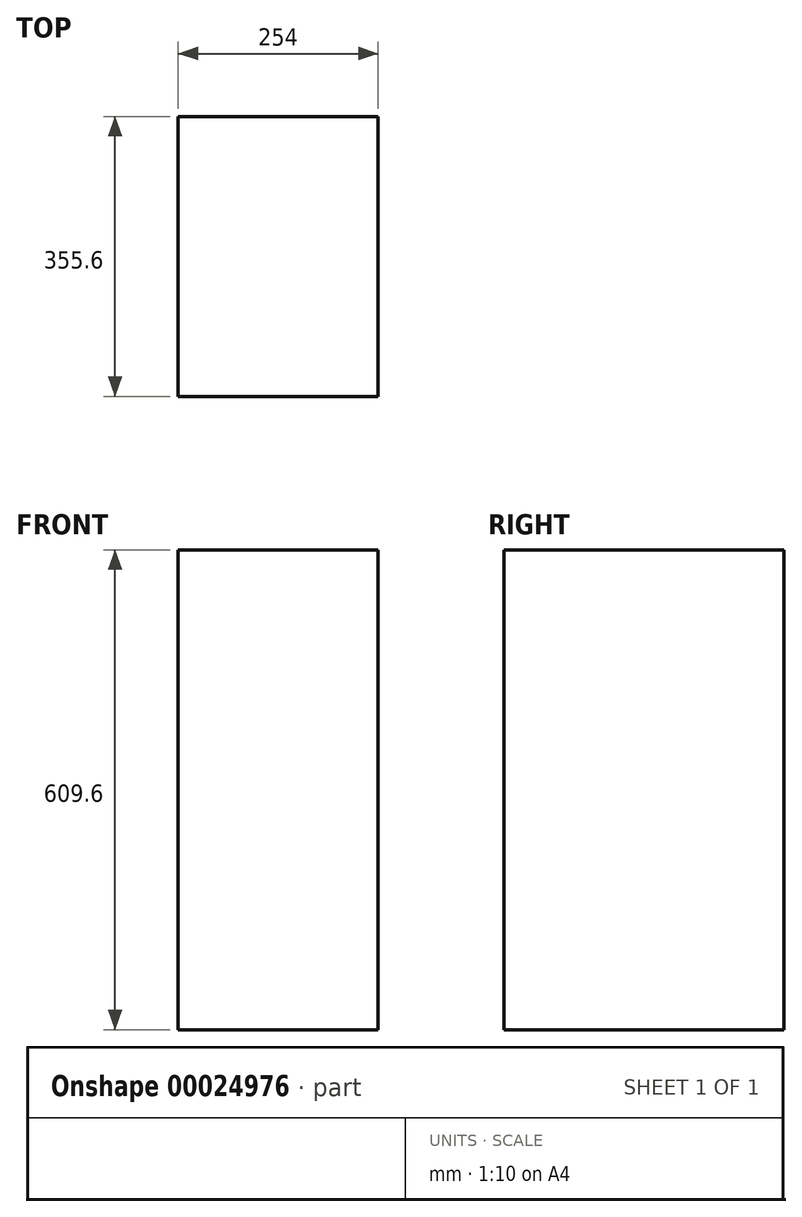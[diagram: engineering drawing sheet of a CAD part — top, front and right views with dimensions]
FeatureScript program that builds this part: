
annotation { "Feature Type Name" : "Feature", "Feature Type Description" : "" }
export const myFeature = defineFeature(function(context is Context, id is Id, definition is map)
    precondition{}
    {
        {
            var Q0;
            Q0=qCreatedBy(makeId("Front.planeOp"),FACE);
            var sketch = newSketch(context, id + "F0", { "sketchPlane" : qUnion([Q0])});
            skLineSegment(sketch, "E0.bottom", {"start": v(-116.58, 557.77) * mm, "end": v(137.42, 557.77) * mm});
            skLineSegment(sketch, "E0.top", {"start": v(-116.58, -51.83) * mm, "end": v(137.42, -51.83) * mm});
            skLineSegment(sketch, "E0.left", {"start": v(-116.58, 557.77) * mm, "end": v(-116.58, -51.83) * mm});
            skLineSegment(sketch, "E0.right", {"start": v(137.42, 557.77) * mm, "end": v(137.42, -51.83) * mm});
            skSolve(sketch);
        }
        {
            var Q0;
            Q0=makeQuery(id+"F0.imprint","IMPRINT",FACE,{"disambiguationData":[TD([[makeQuery(id+"F0.imprint","IMPRINT",EDGE,{"derivedFrom":sQuery(id+"F0.wireOp",EDGE,"E0.bottom")}),-1.0]])]});
            extrude(context, id + "F1", {"entities" : qUnion([Q0]), "depth" : 355.6 * mm});
        }
    });
